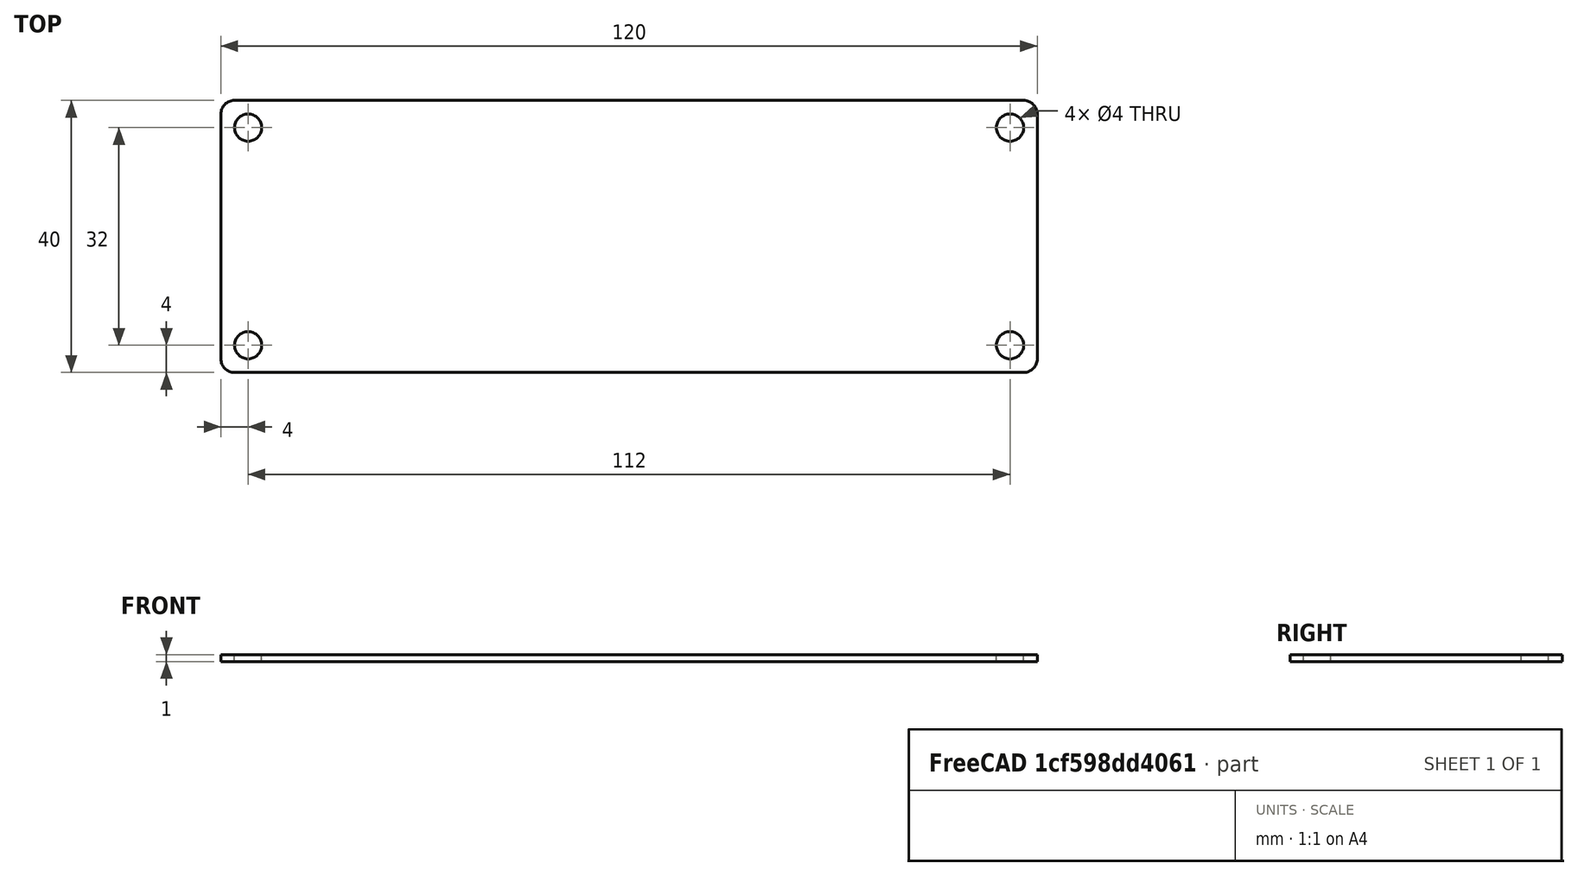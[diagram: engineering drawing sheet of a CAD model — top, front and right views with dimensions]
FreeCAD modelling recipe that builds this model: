
FCSTD DOCUMENT  (FreeCAD 0.18.4R)
Label: Plantilla
License: All rights reserved
LicenseURL: http://en.wikipedia.org/wiki/All_rights_reserved
objects: Part::Box×1, Part::Cylinder×1, Part::FeaturePython×1, Part::Cut×1, Part::Fillet×1, Part::Feature×1
note: 6 computed .brp shape members not serialized (recipe doc carries the construction recipe); baked Part::Feature solids carry a one-line shape summary decoded from their .brp

FEATURE [Part::Box] Box  label="Cubo"
  AttacherType = Attacher::AttachEngine3D
  Height = 1
  Length = 120
  Width = 40
FEATURE [Part::Cylinder] Cylinder  label="Cilindro"
  Angle = 360
  AttacherType = Attacher::AttachEngine3D
  Height = 10
  Placement = pos=(4,4,-1) rot=(0,0,1;0rad)
  Radius = 2
FEATURE [Part::FeaturePython] Array  # Draft array (typed FeaturePython)
  Angle = 360
  ArrayType = 0
  Axis = (0,0,1)
  Base = -> Cylinder
  Center = (0,0,0)
  Fuse = false
  IntervalAxis = (0,0,0)
  IntervalX = (112,0,0)
  IntervalY = (0,32,0)
  IntervalZ = (0,0,1)
  NumberPolar = 1
  NumberX = 2
  NumberY = 2
  NumberZ = 1
FEATURE [Part::Cut] Cut
  Base = -> Box
  Tool = -> Array
FEATURE [Part::Fillet] Fillet
  Base = -> Cut
  Edges = 4 edges r=2: [Edge1,Edge3,Edge6,Edge15]
FEATURE [Part::Feature] Fillet001
  shape: bbox 120 x 40 x 1 mm, 14 faces (baked)
